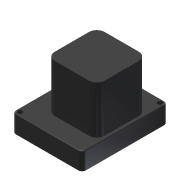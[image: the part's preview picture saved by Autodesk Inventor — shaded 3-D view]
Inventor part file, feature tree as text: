
AUTODESK INVENTOR PART (.ipt)
format: ipt  version: 2013 (Build 170138000, 138)  size: 115,712 bytes
history: native  units: in
note: dims shown in document units (in); Inventor stores cm internally (conversion verified against a paired STEP export)
features: extrude x2, fillet x2, sketch x2
ambient origin geometry x8: Origin, YZ Plane, XZ Plane, XY Plane, X Axis, Y Axis, Z Axis, Center Point
bodies: Solid1 (feature_tree)
feature tree (6):
  extrude  "Extrusion1"  Depth=0.03in
  fillet  "Fillet1"  Radius=1.575in
  extrude  "Extrusion2"  Depth=0.1in
  fillet  "Fillet2"  Radius=1.5in
  sketch  "Sketch2"  dims[d0=0.55in d1=0.0in d2=0.03in d3=1.575in]
  sketch  "Sketch3"  dims[d4=1.575in d5=0.1in d6=1.5in d7=0.0in d8=0.25in]
